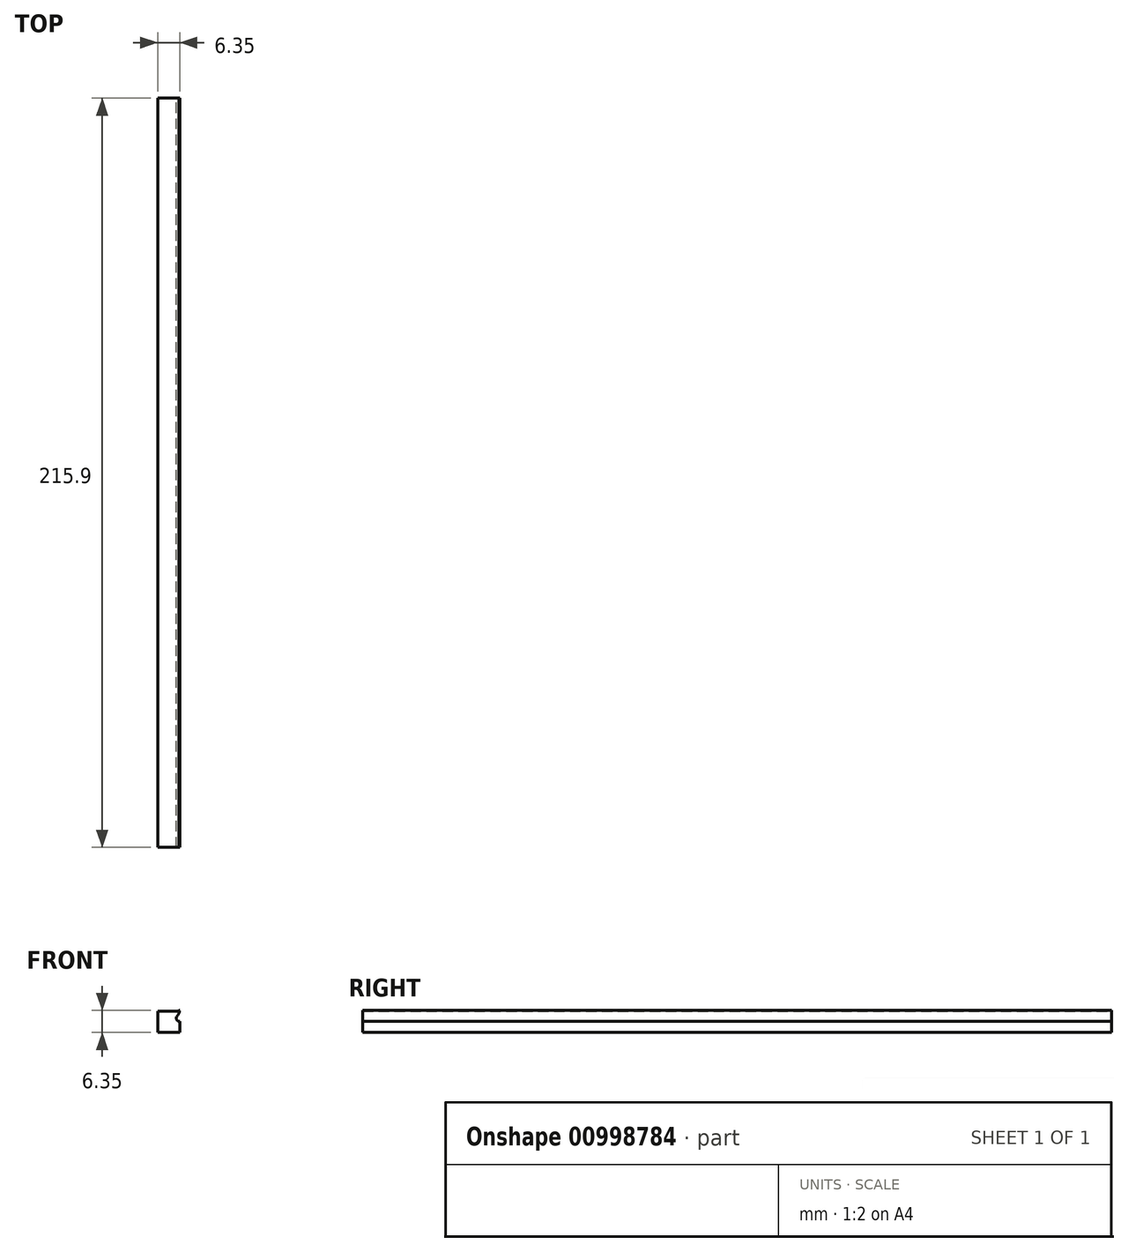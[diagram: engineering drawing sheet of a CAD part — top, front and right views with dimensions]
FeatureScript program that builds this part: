
annotation { "Feature Type Name" : "Feature", "Feature Type Description" : "" }
export const myFeature = defineFeature(function(context is Context, id is Id, definition is map)
    precondition{}
    {
        {
            var Q0;
            Q0=qCreatedBy(makeId("Front.planeOp"),FACE);
            var sketch = newSketch(context, id + "F0", { "sketchPlane" : qUnion([Q0])});
            skLineSegment(sketch, "E0.bottom", {"start": v(4.17, -10.15) * mm, "end": v(16.87, -10.15) * mm});
            skLineSegment(sketch, "E0.top", {"start": v(4.17, -16.5) * mm, "end": v(16.87, -16.5) * mm});
            skLineSegment(sketch, "E0.left", {"start": v(4.17, -10.15) * mm, "end": v(4.17, -16.5) * mm});
            skLineSegment(sketch, "E0.right", {"start": v(16.87, -10.15) * mm, "end": v(16.87, -16.5) * mm});
            skLineSegment(sketch, "E1", {"start": v(4.17, -16.5) * mm, "end": v(4.17, -13.32) * mm});
            skLineSegment(sketch, "E2", {"start": v(4.17, -10.15) * mm, "end": v(4.17, -11.42) * mm});
            skLineSegment(sketch, "E3", {"start": v(4.17, -11.42) * mm, "end": v(4.17, -13.32) * mm});
            skLineSegment(sketch, "E4", {"start": v(4.17, -11.42) * mm, "end": v(4.17, -12.37) * mm});
            skLineSegment(sketch, "E5", {"start": v(4.17, -12.37) * mm, "end": v(5.13, -12.37) * mm});
            skCircle(sketch, "E6", {"center": v(4.17, -12.37) * mm, "radius": 0.95 * mm});
            skLineSegment(sketch, "E7", {"start": v(10.52, -10.15) * mm, "end": v(10.52, -16.5) * mm});
            skCircle(sketch, "E8.MirrorC", {"center": v(16.87, -12.37) * mm, "radius": 0.95 * mm});
            skSolve(sketch);
        }
        {
            var Q0;
            {var subQ1=sQuery(id+"F0.wireOp",EDGE,"E1");Q0=makeQuery(id+"F0.imprint","IMPRINT",FACE,{"disambiguationData":[TD([[makeQuery(id+"F0.imprint","IMPRINT",EDGE,{"derivedFrom":subQ1}),-1.0]])]});}
            var Q1;
            {var subQ5=sQuery(id+"F0.wireOp",EDGE,"E7");Q1=makeQuery(id+"F0.imprint","IMPRINT",FACE,{"disambiguationData":[TD([[makeQuery(id+"F0.imprint","IMPRINT",EDGE,{"derivedFrom":subQ5}),1.0]])]});}
            extrude(context, id + "F1", {"entities" : qUnion([Q0, Q1]), "depth" : 215.9 * mm, "offsetDistance" : 25.4 * mm});
        }
        {
            var Q0;
            {var subQ0=sQuery(id+"F0.wireOp",EDGE,"E8.MirrorC");var subQ1=sQuery(id+"F0.wireOp",EDGE,"E0.right");Q0=makeQuery(id+"F1.opExtrude","SWEPT_EDGE",EDGE,{"disambiguationData":[OSD([subQ1,subQ0]),TDD([makeQuery(id+"F0.imprint","INTERSECT",VERTEX,{"disambiguationData":[OD(1.0)],"derivedFrom":[subQ1,subQ0]})])]});}
            var Q1;
            Q1=makeQuery(id+"F1.opExtrude","SWEPT_EDGE",EDGE,{"disambiguationData":[OSD([sQuery(id+"F0.wireOp",EDGE,"E1"),sQuery(id+"F0.wireOp",EDGE,"E3"),sQuery(id+"F0.wireOp",EDGE,"E6")])]});
            fillet(context, id + "F2", {"entities" : qUnion([Q0, Q1]), "radius" : 2.54 * mm, "tangentPropagation" : true, "allowEdgeOverflow" : false});
        }
        {
            var Q0;
            Q0=makeQuery(id+"F1.opExtrude","CAP_FACE",FACE,{"disambiguationData":[OSD([sQuery(id+"F0.wireOp",EDGE,"E0.bottom"),sQuery(id+"F0.wireOp",EDGE,"E0.top"),sQuery(id+"F0.wireOp",EDGE,"E0.right"),sQuery(id+"F0.wireOp",EDGE,"E1"),sQuery(id+"F0.wireOp",EDGE,"E2"),sQuery(id+"F0.wireOp",EDGE,"E6"),sQuery(id+"F0.wireOp",EDGE,"E8.MirrorC")])],"isStart":false});
            var sketch = newSketch(context, id + "F3", { "sketchPlane" : qUnion([Q0])});
            skLineSegment(sketch, "E9.bottom", {"start": v(4.17, -10.15) * mm, "end": v(4.42, -10.15) * mm});
            skLineSegment(sketch, "E9.top", {"start": v(4.17, -10.4) * mm, "end": v(4.42, -10.4) * mm});
            skLineSegment(sketch, "E9.left", {"start": v(4.17, -10.15) * mm, "end": v(4.17, -10.4) * mm});
            skLineSegment(sketch, "E9.right", {"start": v(4.42, -10.15) * mm, "end": v(4.42, -10.4) * mm});
            skLineSegment(sketch, "E10.bottom", {"start": v(16.87, -10.15) * mm, "end": v(16.61, -10.15) * mm});
            skLineSegment(sketch, "E10.top", {"start": v(16.87, -10.4) * mm, "end": v(16.61, -10.4) * mm});
            skLineSegment(sketch, "E10.left", {"start": v(16.87, -10.15) * mm, "end": v(16.87, -10.4) * mm});
            skLineSegment(sketch, "E10.right", {"start": v(16.61, -10.15) * mm, "end": v(16.61, -10.4) * mm});
            skLineSegment(sketch, "E11", {"start": v(4.42, -10.4) * mm, "end": v(16.61, -10.4) * mm});
            skLineSegment(sketch, "E12.bottom", {"start": v(4.42, -10.15) * mm, "end": v(16.61, -10.15) * mm});
            skSolve(sketch);
        }
        {
            var Q0;
            Q0=makeQuery(id+"F3.imprint","IMPRINT",FACE,{"disambiguationData":[TD([[makeQuery(id+"F3.imprint","IMPRINT",EDGE,{"derivedFrom":sQuery(id+"F3.wireOp",EDGE,"E12.bottom")}),-1.0]])]});
            extrude(context, id + "F4", {"entities" : qUnion([Q0]), "operationType" : NewBodyOperationType.REMOVE, "endBound" : BoundingType.THROUGH_ALL, "oppositeDirection" : true, "depth" : 25.4 * mm, "offsetDistance" : 25.4 * mm});
        }
        {
            var Q0;
            Q0=makeQuery(id+"F4.boolean.opBoolean","COPY",EDGE,{"derivedFrom":makeQuery(id+"F4.opExtrude","SWEPT_EDGE",EDGE,{"disambiguationData":[OSD([sQuery(id+"F3.wireOp",EDGE,"E9.top"),sQuery(id+"F3.wireOp",EDGE,"E11"),sQuery(id+"F3.wireOp",EDGE,"E9.right")])]})});
            var Q1;
            Q1=makeQuery(id+"F4.boolean.opBoolean","COPY",EDGE,{"derivedFrom":makeQuery(id+"F4.opExtrude","SWEPT_EDGE",EDGE,{"disambiguationData":[OSD([sQuery(id+"F3.wireOp",EDGE,"E10.top"),sQuery(id+"F3.wireOp",EDGE,"E11"),sQuery(id+"F3.wireOp",EDGE,"E10.right")])]})});
            var Q2;
            Q2=makeQuery(id+"F1.opExtrude","SWEPT_EDGE",EDGE,{"disambiguationData":[OSD([sQuery(id+"F0.wireOp",EDGE,"E0.bottom"),sQuery(id+"F0.wireOp",EDGE,"E0.right")])]});
            var Q3;
            Q3=makeQuery(id+"F1.opExtrude","SWEPT_EDGE",EDGE,{"disambiguationData":[OSD([sQuery(id+"F0.wireOp",EDGE,"E0.bottom"),sQuery(id+"F0.wireOp",EDGE,"E2")])]});
            fillet(context, id + "F5", {"entities" : qUnion([Q0, Q1, Q2, Q3]), "radius" : 0.25 * mm, "tangentPropagation" : true, "allowEdgeOverflow" : false});
        }
    });
